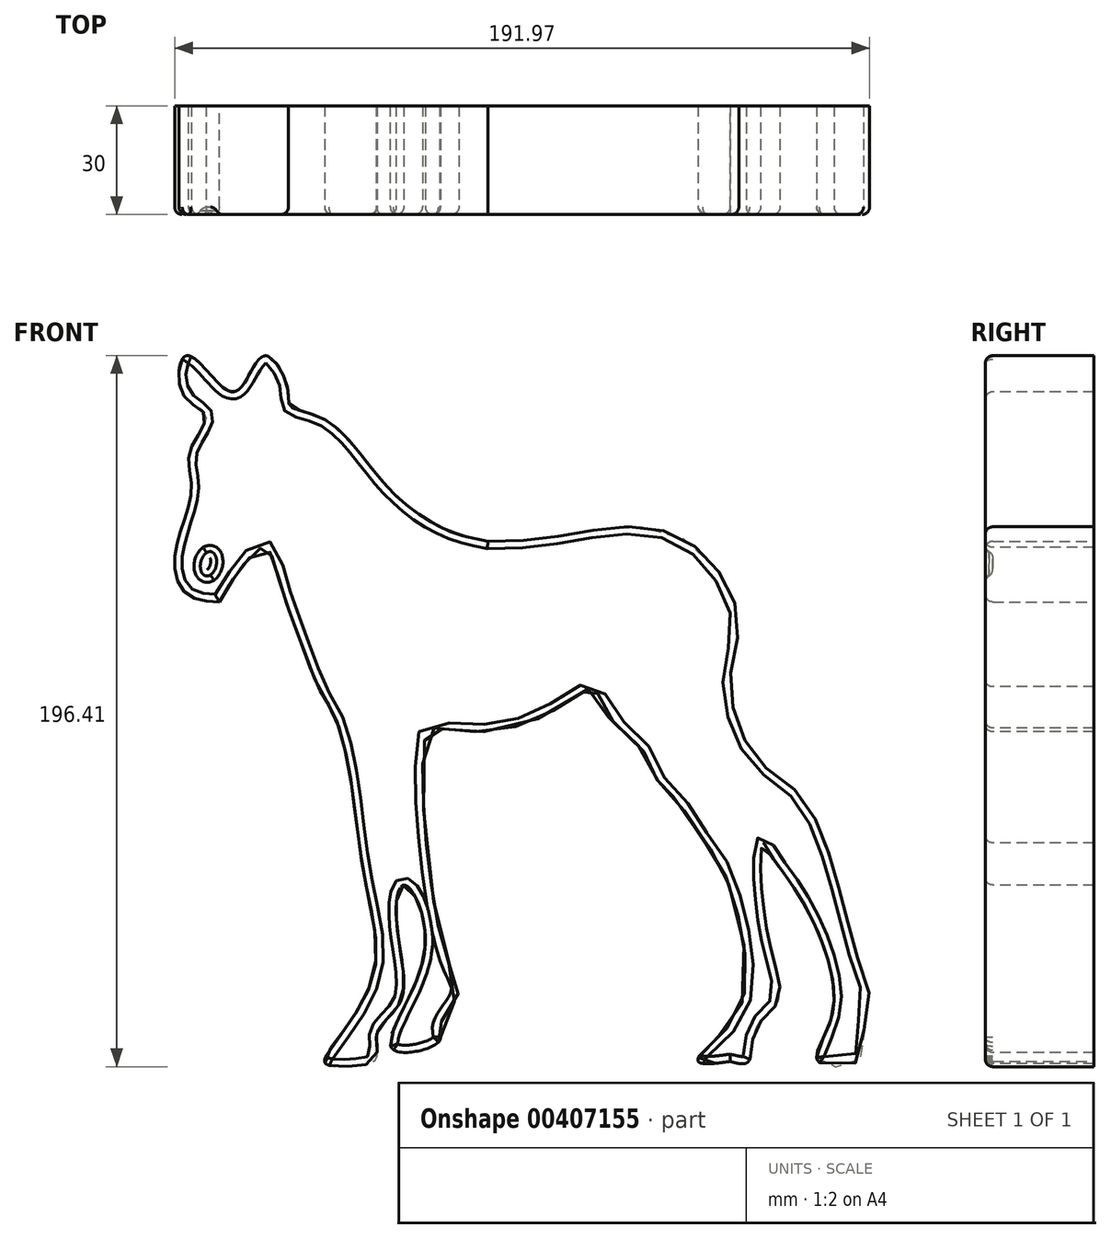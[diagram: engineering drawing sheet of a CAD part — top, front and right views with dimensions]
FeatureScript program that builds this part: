
annotation { "Feature Type Name" : "Feature", "Feature Type Description" : "" }
export const myFeature = defineFeature(function(context is Context, id is Id, definition is map)
    precondition{}
    {
        {
            var Q0;
            Q0=qCreatedBy(makeId("Front.planeOp"),FACE);
            var sketch = newSketch(context, id + "F0", { "sketchPlane" : qUnion([Q0])});
            skFitSpline(sketch, "E0", {"points": [v(-70.05, 11.42) * mm, v(-65.23, 19.07) * mm, v(-57.58, 26.44) * mm, v(-53.61, 17.94) * mm, v(-47.38, 0) * mm, v(-41.71, -14.09) * mm, v(-38.88, -18.62) * mm, v(-34.34, -33.92) * mm, v(-30.1, -63.96) * mm, v(-26.7, -87.2) * mm, v(-31.8, -101.36) * mm, v(-38.03, -110.15) * mm, v(-40.86, -115.82) * mm, v(-34.52, -116.92) * mm, v(-26.7, -114.68) * mm, v(-26.4, -107.6) * mm, v(-19.9, -98.81) * mm, v(-21.02, -77.56) * mm, v(-19.04, -66.8) * mm, v(-13.37, -85.5) * mm, v(-22.16, -112.13) * mm, v(-9.4, -110.15) * mm, v(-9.12, -105.9) * mm, v(-4.02, -96.83) * mm, v(-7.42, -86.35) * mm, v(-12.8, -24.85) * mm, v(-8.56, -23.72) * mm, v(15.81, -21.74) * mm, v(33.95, -12.1) * mm, v(35.08, -16.92) * mm, v(46.99, -29.67) * mm, v(51.52, -38.74) * mm, v(55.77, -42.7) * mm, v(62.57, -52.9) * mm, v(68.8, -61.98) * mm, v(74.76, -98.25) * mm, v(64.84, -111.28) * mm, v(62.29, -115.53) * mm, v(71.07, -115.53) * mm], "startDerivative": vector(185.17, 317.08) * mm, "endDerivative": vector(565.5, 75.45) * mm});
            skFitSpline(sketch, "E1", {"points": [v(71.07, -115.53) * mm, v(76.17, -115.53) * mm, v(78.16, -106.47) * mm, v(84.4, -98.81) * mm, v(81.27, -79.54) * mm, v(80.14, -55.17) * mm, v(81.84, -57.73) * mm, v(90.06, -69.63) * mm, v(99.41, -101.93) * mm, v(95.44, -115.53) * mm, v(106.5, -115.53) * mm, v(107.91, -108.45) * mm, v(109.61, -98.25) * mm, v(106.78, -88.61) * mm, v(92.33, -44.4) * mm, v(78.72, -32.22) * mm, v(71.07, -9.83) * mm, v(73.34, 7.17) * mm, v(55.49, 30.12) * mm, v(22.05, 29.27) * mm, v(4.2, 28.14) * mm], "startDerivative": vector(221.87, -59.25) * mm, "endDerivative": vector(-305.98, -0.38) * mm});
            skFitSpline(sketch, "E2", {"points": [v(4.2, 28.14) * mm, v(-7.14, 31.25) * mm, v(-23.57, 43.16) * mm, v(-40.58, 61.58) * mm, v(-50.5, 65.54) * mm, v(-51.06, 70.08) * mm, v(-57.3, 79.4) * mm, v(-63.81, 70.93) * mm, v(-68.63, 70.36) * mm, v(-79.12, 79.4) * mm, v(-79.97, 68.66) * mm, v(-73.73, 62.7) * mm, v(-78.27, 52.8) * mm, v(-77.7, 42.59) * mm, v(-82.2, 24.74) * mm, v(-79.12, 13.69) * mm, v(-70.05, 11.42) * mm], "startDerivative": vector(-171.6, 33.2) * mm, "endDerivative": vector(178.7, -9.5) * mm});
            skSolve(sketch);
        }
        {
            var Q0;
            Q0 = qSketchRegion(id + "F0", true);
            extrude(context, id + "F1", {"entities" : qUnion([Q0]), "depth" : 30 * mm});
        }
        {
            var Q0;
            Q0=makeQuery(id+"F1.opExtrude","CAP_FACE",FACE,{"disambiguationData":[OSD([sQuery(id+"F0.wireOp",EDGE,"E0"),sQuery(id+"F0.wireOp",EDGE,"E1"),sQuery(id+"F0.wireOp",EDGE,"E2")])],"isStart":false});
            var sketch = newSketch(context, id + "F2", { "sketchPlane" : qUnion([Q0])});
            skEllipse(sketch, "E3", {"center": v(-73, 21.93) * mm, "majorRadius": 3.67 * mm, "minorRadius": 2.43 * mm, "majorAxis": v(0.21, 0.98)});
            skSolve(sketch);
        }
        {
            var Q0;
            Q0 = qSketchRegion(id + "F2", true);
            extrude(context, id + "F3", {"entities" : qUnion([Q0]), "operationType" : NewBodyOperationType.REMOVE, "oppositeDirection" : true, "depth" : 2 * mm});
        }
        {
            var Q0;
            Q0=makeQuery(id+"F3.boolean.opBoolean","COPY",EDGE,{"derivedFrom":makeQuery(id+"F3.opExtrude","CAP_EDGE",EDGE,{"disambiguationData":[OSD([sQuery(id+"F2.wireOp",EDGE,"E3")])],"isStart":false})});
            fillet(context, id + "F4", {"entities" : qUnion([Q0]), "radius" : 1.9 * mm, "tangentPropagation" : true, "allowEdgeOverflow" : false});
        }
        {
            var Q0;
            Q0=makeQuery(id+"F1.opExtrude","CAP_FACE",FACE,{"disambiguationData":[OSD([sQuery(id+"F0.wireOp",EDGE,"E0"),sQuery(id+"F0.wireOp",EDGE,"E1"),sQuery(id+"F0.wireOp",EDGE,"E2")])],"isStart":false});
            fillet(context, id + "F5", {"entities" : qUnion([Q0]), "radius" : 2 * mm, "tangentPropagation" : true, "allowEdgeOverflow" : false});
        }
    });
